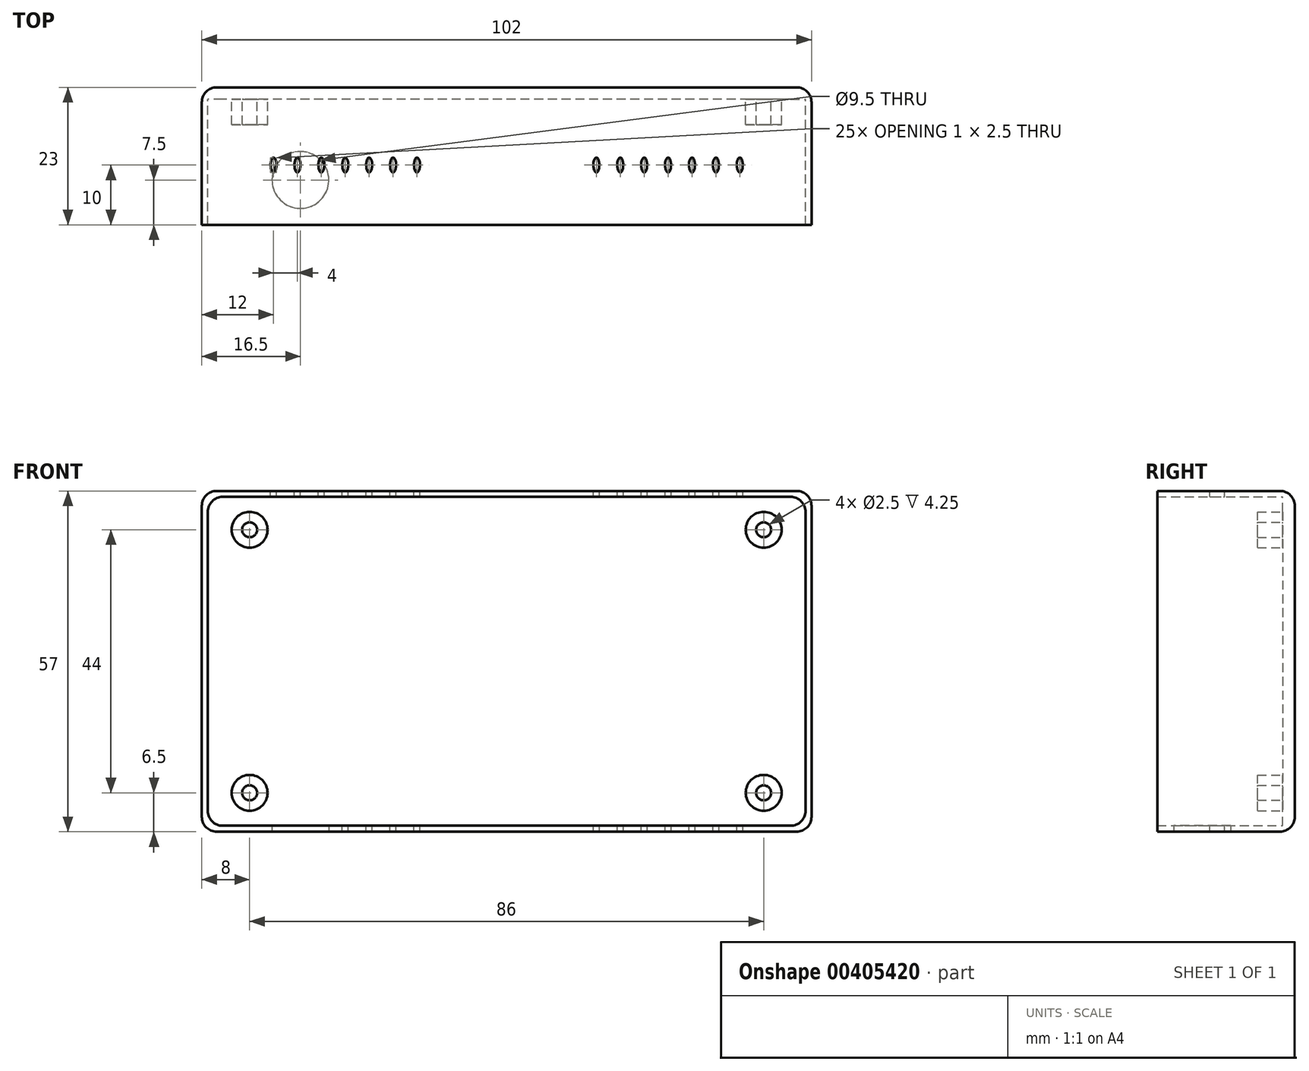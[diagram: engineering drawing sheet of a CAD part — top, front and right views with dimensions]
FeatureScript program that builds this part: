
annotation { "Feature Type Name" : "Feature", "Feature Type Description" : "" }
export const myFeature = defineFeature(function(context is Context, id is Id, definition is map)
    precondition{}
    {
        {
            var Q0;
            Q0=qCreatedBy(makeId("Front.planeOp"),FACE);
            var sketch = newSketch(context, id + "F0", { "sketchPlane" : qUnion([Q0])});
            skLineSegment(sketch, "E0.bottom", {"start": v(50, 27.5) * mm, "end": v(-50, 27.5) * mm});
            skLineSegment(sketch, "E0.top", {"start": v(50, -27.5) * mm, "end": v(-50, -27.5) * mm});
            skLineSegment(sketch, "E0.left", {"start": v(50, 27.5) * mm, "end": v(50, -27.5) * mm});
            skLineSegment(sketch, "E0.right", {"start": v(-50, 27.5) * mm, "end": v(-50, -27.5) * mm});
            skPoint(sketch, "E0.middle", {"position": v(0, 0) * mm});
            skLineSegment(sketch, "E1.bottom", {"start": v(-51, 28.5) * mm, "end": v(51, 28.5) * mm});
            skLineSegment(sketch, "E1.top", {"start": v(-51, -28.5) * mm, "end": v(51, -28.5) * mm});
            skLineSegment(sketch, "E1.left", {"start": v(-51, 28.5) * mm, "end": v(-51, -28.5) * mm});
            skLineSegment(sketch, "E1.right", {"start": v(51, 28.5) * mm, "end": v(51, -28.5) * mm});
            skSolve(sketch);
        }
        {
            var Q0;
            Q0=makeQuery(id+"F0.imprint","IMPRINT",FACE,{"disambiguationData":[TD([[makeQuery(id+"F0.imprint","IMPRINT",EDGE,{"derivedFrom":sQuery(id+"F0.wireOp",EDGE,"E0.bottom")}),1.0]])]});
            var sketch = newSketch(context, id + "F1", { "sketchPlane" : qUnion([Q0])});
            skLineSegment(sketch, "E2.bottom", {"start": v(-43, -22) * mm, "end": v(43, -22) * mm, "construction": true});
            skLineSegment(sketch, "E2.top", {"start": v(-43, 22) * mm, "end": v(43, 22) * mm, "construction": true});
            skLineSegment(sketch, "E2.left", {"start": v(-43, -22) * mm, "end": v(-43, 22) * mm, "construction": true});
            skLineSegment(sketch, "E2.right", {"start": v(43, -22) * mm, "end": v(43, 22) * mm, "construction": true});
            skPoint(sketch, "E2.middle", {"position": v(0, 0) * mm});
            skCircle(sketch, "E3", {"center": v(-43, 22) * mm, "radius": 1.25 * mm});
            skCircle(sketch, "E4", {"center": v(-43, 22) * mm, "radius": 3 * mm});
            skCircle(sketch, "E5", {"center": v(-43, -22) * mm, "radius": 1.25 * mm});
            skCircle(sketch, "E6", {"center": v(-43, -22) * mm, "radius": 3 * mm});
            skCircle(sketch, "E7", {"center": v(43, -22) * mm, "radius": 1.25 * mm});
            skCircle(sketch, "E8", {"center": v(43, -22) * mm, "radius": 3 * mm});
            skCircle(sketch, "E9", {"center": v(43, 22) * mm, "radius": 1.25 * mm});
            skCircle(sketch, "E10", {"center": v(43, 22) * mm, "radius": 3 * mm});
            skLineSegment(sketch, "E11.bottom", {"start": v(-43, -22) * mm, "end": v(-34.5, -22) * mm, "construction": true});
            skLineSegment(sketch, "E11.top", {"start": v(-43, -31.16) * mm, "end": v(-34.5, -31.16) * mm, "construction": true});
            skLineSegment(sketch, "E11.left", {"start": v(-43, -22) * mm, "end": v(-43, -31.16) * mm, "construction": true});
            skLineSegment(sketch, "E11.right", {"start": v(-34.5, -22) * mm, "end": v(-34.5, -31.16) * mm, "construction": true});
            skSolve(sketch);
        }
        {
            var Q0;
            Q0=makeQuery(id+"F0.imprint","IMPRINT",FACE,{"disambiguationData":[TD([[makeQuery(id+"F0.imprint","IMPRINT",EDGE,{"derivedFrom":sQuery(id+"F0.wireOp",EDGE,"E0.bottom")}),-1.0]])]});
            extrude(context, id + "F2", {"entities" : qUnion([Q0]), "depth" : 23 * mm});
        }
        {
            var Q0;
            Q0=makeQuery(id+"F0.imprint","IMPRINT",FACE,{"disambiguationData":[TD([[makeQuery(id+"F0.imprint","IMPRINT",EDGE,{"derivedFrom":sQuery(id+"F0.wireOp",EDGE,"E0.bottom")}),1.0]])]});
            var Q1;
            Q1=makeQuery(id+"F1.imprint","IMPRINT",FACE,{"disambiguationData":[TD([[makeQuery(id+"F1.imprint","IMPRINT",EDGE,{"derivedFrom":sQuery(id+"F1.wireOp",EDGE,"E9")}),-1.0]])]});
            var Q2;
            Q2=makeQuery(id+"F1.imprint","IMPRINT",FACE,{"disambiguationData":[TD([[makeQuery(id+"F1.imprint","IMPRINT",EDGE,{"derivedFrom":sQuery(id+"F1.wireOp",EDGE,"E4")}),-1.0]])]});
            extrude(context, id + "F3", {"entities" : qUnion([Q0, Q1, Q2]), "operationType" : NewBodyOperationType.ADD, "depth" : 2 * mm});
        }
        {
            var Q0;
            Q0=makeQuery(id+"F2.opExtrude","CAP_EDGE",EDGE,{"disambiguationData":[OSD([sQuery(id+"F0.wireOp",EDGE,"E1.top")])],"isStart":true});
            var Q1;
            Q1=makeQuery(id+"F2.opExtrude","CAP_EDGE",EDGE,{"disambiguationData":[OSD([sQuery(id+"F0.wireOp",EDGE,"E1.bottom")])],"isStart":true});
            var Q2;
            Q2=makeQuery(id+"F2.opExtrude","CAP_EDGE",EDGE,{"disambiguationData":[OSD([sQuery(id+"F0.wireOp",EDGE,"E1.left")])],"isStart":true});
            var Q3;
            Q3=makeQuery(id+"F2.opExtrude","CAP_EDGE",EDGE,{"disambiguationData":[OSD([sQuery(id+"F0.wireOp",EDGE,"E1.right")])],"isStart":true});
            fillet(context, id + "F4", {"entities" : qUnion([Q0, Q1, Q2, Q3]), "radius" : 2.5 * mm, "tangentPropagation" : true, "allowEdgeOverflow" : false});
        }
        {
            var Q0;
            Q0=makeQuery(id+"F2.opExtrude","SWEPT_EDGE",EDGE,{"disambiguationData":[OSD([sQuery(id+"F0.wireOp",EDGE,"E1.bottom"),sQuery(id+"F0.wireOp",EDGE,"E1.left")])]});
            var Q1;
            Q1=makeQuery(id+"F2.opExtrude","SWEPT_EDGE",EDGE,{"disambiguationData":[OSD([sQuery(id+"F0.wireOp",EDGE,"E1.bottom"),sQuery(id+"F0.wireOp",EDGE,"E1.right")])]});
            var Q2;
            Q2=makeQuery(id+"F2.opExtrude","SWEPT_EDGE",EDGE,{"disambiguationData":[OSD([sQuery(id+"F0.wireOp",EDGE,"E1.top"),sQuery(id+"F0.wireOp",EDGE,"E1.right")])]});
            var Q3;
            Q3=makeQuery(id+"F2.opExtrude","SWEPT_EDGE",EDGE,{"disambiguationData":[OSD([sQuery(id+"F0.wireOp",EDGE,"E1.top"),sQuery(id+"F0.wireOp",EDGE,"E1.left")])]});
            fillet(context, id + "F5", {"entities" : qUnion([Q0, Q1, Q2, Q3]), "radius" : 2.5 * mm, "tangentPropagation" : true, "allowEdgeOverflow" : false});
        }
        {
            var Q0;
            Q0=makeQuery(id+"F2.opExtrude","SWEPT_EDGE",EDGE,{"disambiguationData":[OSD([sQuery(id+"F0.wireOp",EDGE,"E0.top"),sQuery(id+"F0.wireOp",EDGE,"E0.right")])]});
            var Q1;
            Q1=makeQuery(id+"F2.opExtrude","SWEPT_EDGE",EDGE,{"disambiguationData":[OSD([sQuery(id+"F0.wireOp",EDGE,"E0.bottom"),sQuery(id+"F0.wireOp",EDGE,"E0.right")])]});
            var Q2;
            Q2=makeQuery(id+"F2.opExtrude","SWEPT_EDGE",EDGE,{"disambiguationData":[OSD([sQuery(id+"F0.wireOp",EDGE,"E0.bottom"),sQuery(id+"F0.wireOp",EDGE,"E0.left")])]});
            var Q3;
            Q3=makeQuery(id+"F2.opExtrude","SWEPT_EDGE",EDGE,{"disambiguationData":[OSD([sQuery(id+"F0.wireOp",EDGE,"E0.top"),sQuery(id+"F0.wireOp",EDGE,"E0.left")])]});
            fillet(context, id + "F6", {"entities" : qUnion([Q0, Q1, Q2, Q3]), "radius" : 2.5 * mm, "tangentPropagation" : true, "allowEdgeOverflow" : false});
        }
        {
            var Q0;
            Q0 = qSketchRegion(id + "F1", true);
            extrude(context, id + "F7", {"entities" : qUnion([Q0]), "operationType" : NewBodyOperationType.ADD, "depth" : 6.25 * mm});
        }
        {
            var Q0;
            Q0=makeQuery(id+"F2.opExtrude","SWEPT_FACE",FACE,{"disambiguationData":[OSD([sQuery(id+"F0.wireOp",EDGE,"E1.bottom")])]});
            var sketch = newSketch(context, id + "F8", { "sketchPlane" : qUnion([Q0])});
            skLineSegment(sketch, "E12", {"start": v(0, 0) * mm, "end": v(0, -12) * mm});
            skEllipse(sketch, "E13", {"center": v(-39, -13) * mm, "majorRadius": 0.5 * mm, "minorRadius": 1.25 * mm, "majorAxis": v(-1, 0)});
            skEllipse(sketch, "E14", {"center": v(39, -13) * mm, "majorRadius": 0.5 * mm, "minorRadius": 1.25 * mm, "majorAxis": v(-1, 0)});
            skEllipse(sketch, "E15", {"center": v(-35, -13) * mm, "majorRadius": 0.5 * mm, "minorRadius": 1.25 * mm, "majorAxis": v(-1, 0)});
            skEllipse(sketch, "E16", {"center": v(-31, -13) * mm, "majorRadius": 0.5 * mm, "minorRadius": 1.25 * mm, "majorAxis": v(-1, 0)});
            skEllipse(sketch, "E17", {"center": v(27, -13) * mm, "majorRadius": 0.5 * mm, "minorRadius": 1.25 * mm, "majorAxis": v(-1, 0)});
            skEllipse(sketch, "E18", {"center": v(23, -13) * mm, "majorRadius": 0.5 * mm, "minorRadius": 1.25 * mm, "majorAxis": v(-1, 0)});
            skEllipse(sketch, "E19", {"center": v(19, -13) * mm, "majorRadius": 0.5 * mm, "minorRadius": 1.25 * mm, "majorAxis": v(-1, 0)});
            skEllipse(sketch, "E20", {"center": v(15, -13) * mm, "majorRadius": 0.5 * mm, "minorRadius": 1.25 * mm, "majorAxis": v(-1, 0)});
            skEllipse(sketch, "E21", {"center": v(-27, -13) * mm, "majorRadius": 0.5 * mm, "minorRadius": 1.25 * mm, "majorAxis": v(-1, 0)});
            skEllipse(sketch, "E22", {"center": v(-19, -13) * mm, "majorRadius": 0.5 * mm, "minorRadius": 1.25 * mm, "majorAxis": v(-1, 0)});
            skEllipse(sketch, "E23", {"center": v(-15, -13) * mm, "majorRadius": 0.5 * mm, "minorRadius": 1.25 * mm, "majorAxis": v(-1, 0)});
            skEllipse(sketch, "E24", {"center": v(31, -13) * mm, "majorRadius": 0.5 * mm, "minorRadius": 1.25 * mm, "majorAxis": v(-1, 0)});
            skEllipse(sketch, "E25", {"center": v(35, -13) * mm, "majorRadius": 0.5 * mm, "minorRadius": 1.25 * mm, "majorAxis": v(-1, 0)});
            skEllipse(sketch, "E26", {"center": v(-23, -13) * mm, "majorRadius": 0.5 * mm, "minorRadius": 1.25 * mm, "majorAxis": v(-1, 0)});
            skSolve(sketch);
        }
        {
            var Q0;
            Q0=makeQuery(id+"F8.imprint","IMPRINT",FACE,{"disambiguationData":[TD([[makeQuery(id+"F8.imprint","IMPRINT",EDGE,{"derivedFrom":sQuery(id+"F8.wireOp",EDGE,"E20")}),1.0]])]});
            var Q1;
            Q1=makeQuery(id+"F8.imprint","IMPRINT",FACE,{"disambiguationData":[TD([[makeQuery(id+"F8.imprint","IMPRINT",EDGE,{"derivedFrom":sQuery(id+"F8.wireOp",EDGE,"E19")}),1.0]])]});
            var Q2;
            Q2=makeQuery(id+"F8.imprint","IMPRINT",FACE,{"disambiguationData":[TD([[makeQuery(id+"F8.imprint","IMPRINT",EDGE,{"derivedFrom":sQuery(id+"F8.wireOp",EDGE,"E18")}),1.0]])]});
            var Q3;
            Q3=makeQuery(id+"F8.imprint","IMPRINT",FACE,{"disambiguationData":[TD([[makeQuery(id+"F8.imprint","IMPRINT",EDGE,{"derivedFrom":sQuery(id+"F8.wireOp",EDGE,"E17")}),1.0]])]});
            var Q4;
            Q4=makeQuery(id+"F8.imprint","IMPRINT",FACE,{"disambiguationData":[TD([[makeQuery(id+"F8.imprint","IMPRINT",EDGE,{"derivedFrom":sQuery(id+"F8.wireOp",EDGE,"E24")}),1.0]])]});
            var Q5;
            Q5=makeQuery(id+"F8.imprint","IMPRINT",FACE,{"disambiguationData":[TD([[makeQuery(id+"F8.imprint","IMPRINT",EDGE,{"derivedFrom":sQuery(id+"F8.wireOp",EDGE,"E25")}),1.0]])]});
            var Q6;
            Q6=makeQuery(id+"F8.imprint","IMPRINT",FACE,{"disambiguationData":[TD([[makeQuery(id+"F8.imprint","IMPRINT",EDGE,{"derivedFrom":sQuery(id+"F8.wireOp",EDGE,"E14")}),1.0]])]});
            var Q7;
            Q7=makeQuery(id+"F8.imprint","IMPRINT",FACE,{"disambiguationData":[TD([[makeQuery(id+"F8.imprint","IMPRINT",EDGE,{"derivedFrom":sQuery(id+"F8.wireOp",EDGE,"E23")}),1.0]])]});
            var Q8;
            Q8=makeQuery(id+"F8.imprint","IMPRINT",FACE,{"disambiguationData":[TD([[makeQuery(id+"F8.imprint","IMPRINT",EDGE,{"derivedFrom":sQuery(id+"F8.wireOp",EDGE,"E22")}),1.0]])]});
            var Q9;
            Q9=makeQuery(id+"F8.imprint","IMPRINT",FACE,{"disambiguationData":[TD([[makeQuery(id+"F8.imprint","IMPRINT",EDGE,{"derivedFrom":sQuery(id+"F8.wireOp",EDGE,"E26")}),1.0]])]});
            var Q10;
            Q10=makeQuery(id+"F8.imprint","IMPRINT",FACE,{"disambiguationData":[TD([[makeQuery(id+"F8.imprint","IMPRINT",EDGE,{"derivedFrom":sQuery(id+"F8.wireOp",EDGE,"E21")}),1.0]])]});
            var Q11;
            Q11=sQuery(id+"F8.wireOp",EDGE,"E20");
            extrude(context, id + "F9", {"entities" : qUnion([Q0, Q1, Q2, Q3, Q4, Q5, Q6, Q7, Q8, Q9, Q10]), "operationType" : NewBodyOperationType.REMOVE, "surfaceEntities" : qUnion([Q11]), "endBound" : BoundingType.THROUGH_ALL, "oppositeDirection" : true, "depth" : 25 * mm});
        }
        {
            var Q0;
            Q0=makeQuery(id+"F2.opExtrude","SWEPT_FACE",FACE,{"disambiguationData":[OSD([sQuery(id+"F0.wireOp",EDGE,"E1.top")])]});
            var sketch = newSketch(context, id + "F10", { "sketchPlane" : qUnion([Q0])});
            skLineSegment(sketch, "E27", {"start": v(-34.5, 0) * mm, "end": v(-34.5, 15.5) * mm, "construction": true});
            skCircle(sketch, "E28", {"center": v(-34.5, 15.5) * mm, "radius": 4.75 * mm});
            skSolve(sketch);
        }
        {
            var Q0;
            Q0=makeQuery(id+"F8.imprint","IMPRINT",FACE,{"disambiguationData":[TD([[makeQuery(id+"F8.imprint","IMPRINT",EDGE,{"derivedFrom":sQuery(id+"F8.wireOp",EDGE,"E16")}),1.0]])]});
            var Q1;
            Q1=makeQuery(id+"F8.imprint","IMPRINT",FACE,{"disambiguationData":[TD([[makeQuery(id+"F8.imprint","IMPRINT",EDGE,{"derivedFrom":sQuery(id+"F8.wireOp",EDGE,"E15")}),1.0]])]});
            var Q2;
            Q2=makeQuery(id+"F8.imprint","IMPRINT",FACE,{"disambiguationData":[TD([[makeQuery(id+"F8.imprint","IMPRINT",EDGE,{"derivedFrom":sQuery(id+"F8.wireOp",EDGE,"E13")}),1.0]])]});
            extrude(context, id + "F11", {"entities" : qUnion([Q0, Q1, Q2]), "operationType" : NewBodyOperationType.REMOVE, "oppositeDirection" : true, "depth" : 25 * mm, "hasSecondDirection" : true, "secondDirectionOppositeDirection" : false, "secondDirectionDepth" : 10 * mm});
        }
        {
            var Q0;
            Q0=makeQuery(id+"F10.imprint","IMPRINT",FACE,{"disambiguationData":[TD([[makeQuery(id+"F10.imprint","IMPRINT",EDGE,{"derivedFrom":sQuery(id+"F10.wireOp",EDGE,"E28")}),1.0]])]});
            extrude(context, id + "F12", {"entities" : qUnion([Q0]), "operationType" : NewBodyOperationType.REMOVE, "oppositeDirection" : true, "depth" : 10 * mm});
        }
    });
